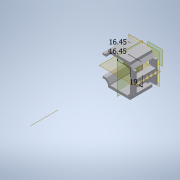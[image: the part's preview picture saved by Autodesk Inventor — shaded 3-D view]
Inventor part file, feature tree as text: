
AUTODESK INVENTOR PART (.ipt)
format: ipt  version: 2022 (Build 260153000, 153)  size: 520,192 bytes
history: native  units: mm
features: reference x24, sketch x12, extrude x11, other x11, projected_geometry x9, plane x8, hole x2, chamfer x1, pattern_circular x1, pattern_linear x1
ambient origin geometry x8: Origin, YZ Plane, XZ Plane, XY Plane, X Axis, Y Axis, Z Axis, Center Point
bodies: Solid1 (feature_tree)
feature tree (80):
  plane  "Work Plane1"
  extrude  "Extrusion1"  Depth=0.1mm
  chamfer  "Chamfer1"  Distance=3.0mm
  sketch  "Sketch2"  dims[d1=0.1mm d2=0.1mm]
  plane  "Work Plane2"
  extrude  "Extrusion2"  Depth=3.001102mm
  other  "Work Axis1"
  pattern_circular  "Circular Pattern1"  Count=4 Angle=360.0deg
  extrude  "Extrusion3"  Depth=1.0mm TaperAngle=0.0deg
  sketch  "Sketch4"  dims[d4=0.1mm]
  plane  "Work Plane3"
  extrude  "Extrusion4"  Depth=2.0mm
  extrude  "Extrusion5"  Depth=2.8mm
  pattern_linear  "Rectangular Pattern1"  Count1=5 Spacing1=6.25mm
  sketch  "Sketch7"  dims[d5=0.1mm]
  plane  "Work Plane4"
  hole  "Hole2"  [1 undecoded]
  plane  "Work Plane6"
  sketch  "Sketch15"  dims[d7=3.0mm d8=3.0mm d9=0.0mm]
  plane  "Work Plane5"
  extrude  "Extrusion12"  Depth=2.0mm
  hole  "Hole3"  [1 undecoded]
  extrude  "Extrusion13"  Depth=2.5mm
  plane  "Work Plane7"
  plane  "Work Plane8"
  extrude  "Extrusion14"  Depth=7.719987mm
  extrude  "Extrusion15"  Depth=10.0mm TaperAngle=0.0deg
  extrude  "Extrusion16"  Depth=49.7mm
  extrude  "Extrusion17"  Depth=2.0mm
  reference  "Reference2"
  reference  "Reference3"
  reference  "Reference4"
  reference  "Reference5"
  projected_geometry  "Projected Loop1"
  sketch  "Sketch3"  dims[d3=0.1mm]
  reference  "Reference8"
  projected_geometry  "Projected Loop2"
  projected_geometry  "Projected Loop3"
  reference  "Reference9"
  reference  "Reference10"
  reference  "Reference11"
  reference  "Reference13"
  reference  "Reference14"
  reference  "Reference15"
  reference  "Reference16"
  projected_geometry  "Projected Loop5"
  reference  "Reference22"
  sketch  "Sketch12"  dims[d6=3.0mm]
  reference  "Reference23"
  reference  "Reference30"
  projected_geometry  "Projected Loop9"
  reference  "Reference32"
  reference  "Reference33"
  reference  "Reference34"
  reference  "Reference35"
  reference  "Reference36"
  sketch  "Sketch16"  dims[d10=3.9mm d11=2.0mm d12=45.0deg d13=3.001102mm]
  reference  "Reference38"
  reference  "Reference39"
  reference  "Reference40"
  reference  "Reference41"
  sketch  "Sketch17"  dims[d14=31.5mm d15=0.0mm d16=40.0mm d17=360.0deg]
  sketch  "Skizze18"  dims[d19=6.0mm d20=1.0mm d21=0.0mm]
  projected_geometry  "Projizierte Kontur10"
  sketch  "Skizze19"  dims[d22=3.0mm d23=0.0mm d24=2.0mm]
  sketch  "Skizze20"  dims[d25=2.8mm d26=2.8mm]
  sketch  "Skizze21"  dims[d27=10.0mm d28=0.0mm d29=50.0mm d31=6.25mm d35=19.0mm d56=2.8mm d57=6.0mm d58=6.0mm d59=3.0mm d60=90.0deg d61=8.0mm d62=20.594885mm d74=16.45mm d75=16.45mm d82=2.5mm d83=7.719987mm d84=10.0mm d85=0.0mm d86=49.7mm d87=24.85mm d88=0.0mm d91=2.8mm d92=6.0mm d93=7.0mm d94=1.0mm d95=90.0deg d96=8.0mm d97=20.594885mm d98=10.0mm d99=0.0mm d100=10.0mm d101=0.0mm d102=34.0mm d103=0.0mm d104=4.0mm d105=4.0mm d106=34.0mm d107=0.0mm d108=2.0mm d109=0.0mm]
  projected_geometry  "Projizierte Kontur11"
  projected_geometry  "Projizierte Kontur12"
  projected_geometry  "Projizierte Kontur13"
  other  "Assembly_Cube_Z_Focus_MGN_NEMA_v3.iam"
  other  "Assembly_Cube_empty_IM_v3:1"
  other  "10_Cube_1x1_IM:2"
  other  "10_Cube_1x1_IM:1"
  other  "DIN 912 - replaced by DIN EN ISO 4762 M3 x 30:1"
  other  "00_MGN12 LINEAR GUIDE RAIL, CONFIGURABLE:1"
  other  "00_NEMA11:1"
  other  "Assembly_Cube_empty_IM_v3:2"
  other  "30_Cube_Z_Focus_MGN_NEMA_rail:1"
  other  "30_Cube_Z_Focus_MGN_NEMA_Motoradapter_NEMA11_v3:1"
note: 2 required parameter values undecoded (feature->parameter linkage not recoverable at this tier; creation-order binding heuristic only, values carry confidence <= 0.55)
